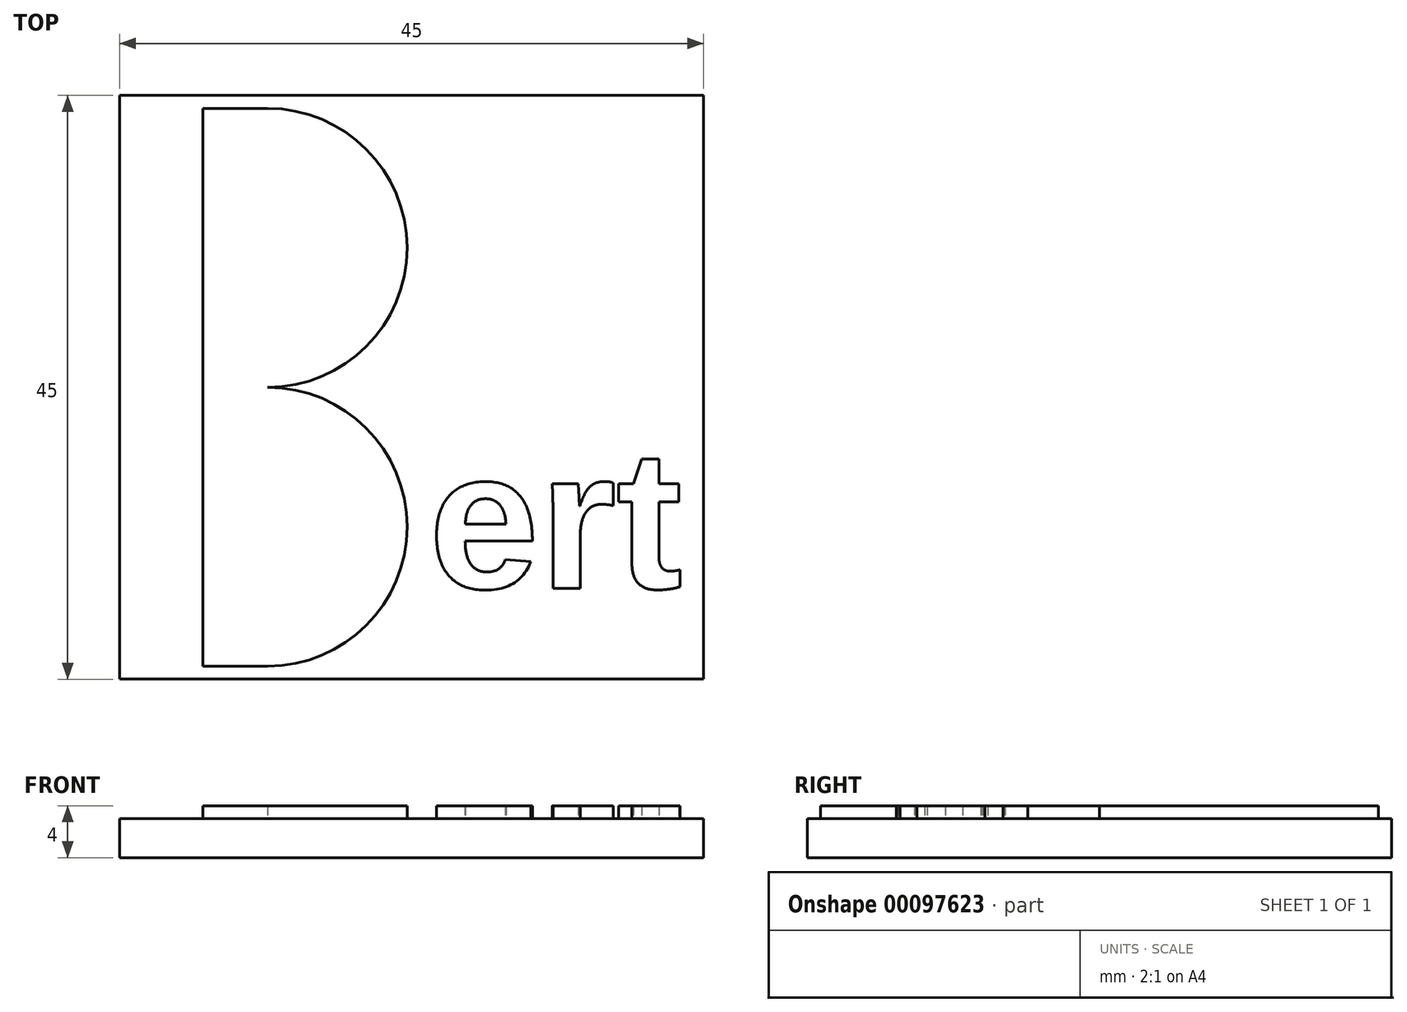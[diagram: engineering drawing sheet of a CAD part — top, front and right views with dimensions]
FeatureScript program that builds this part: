
annotation { "Feature Type Name" : "Feature", "Feature Type Description" : "" }
export const myFeature = defineFeature(function(context is Context, id is Id, definition is map)
    precondition{}
    {
        {
            var Q0;
            Q0=qCreatedBy(makeId("Top.planeOp"),FACE);
            var sketch = newSketch(context, id + "F0", { "sketchPlane" : qUnion([Q0])});
            skLineSegment(sketch, "E0.bottom", {"start": v(-39.88, 12.8) * mm, "end": v(5.12, 12.8) * mm});
            skLineSegment(sketch, "E0.top", {"start": v(-39.88, -32.2) * mm, "end": v(5.12, -32.2) * mm});
            skLineSegment(sketch, "E0.left", {"start": v(-39.88, 12.8) * mm, "end": v(-39.88, -32.2) * mm});
            skLineSegment(sketch, "E0.right", {"start": v(5.12, 12.8) * mm, "end": v(5.12, -32.2) * mm});
            skPoint(sketch, "E1", {"position": v(-33.48, 12.8) * mm});
            skLineSegment(sketch, "E2", {"start": v(-33.48, 11.8) * mm, "end": v(-33.48, -31.2) * mm});
            skLineSegment(sketch, "E3", {"start": v(-33.48, 11.8) * mm, "end": v(-28.48, 11.8) * mm});
            skLineSegment(sketch, "E4", {"start": v(-33.48, -31.2) * mm, "end": v(-28.48, -31.2) * mm});
            skArc(sketch, "E5", {"start": v(-28.48, -31.2) * mm, "mid": v(-17.73, -20.46) * mm, "end": v(-28.48, -9.7) * mm});
            skText(sketch, "E6", { "text": "ert", "fontName": "Arimo-Bold.ttf"});
            skArc(sketch, "E7", {"start": v(-28.48, -9.7) * mm, "mid": v(-17.73, 1.04) * mm, "end": v(-28.48, 11.8) * mm});
            skPoint(sketch, "E8.orphan", {"position": v(-28.48, 11.8) * mm});
            skPoint(sketch, "E9.orphan", {"position": v(-28.48, -9.7) * mm});
            const initialGuessF0  = {"E6": [-0.01605, -0.0252, 1, 0, 0.011]};
            skSetInitialGuess(sketch, initialGuessF0);
            skSolve(sketch);
        }
        {
            var Q0;
            Q0=makeQuery(id+"F0.imprint","IMPRINT",FACE,{"disambiguationData":[TD([[makeQuery(id+"F0.imprint","IMPRINT",EDGE,{"derivedFrom":sQuery(id+"F0.wireOp",EDGE,"E2")}),1.0]])]});
            var Q1;
            Q1=makeQuery(id+"F0.imprint","IMPRINT",FACE,{"disambiguationData":[TD([[makeQuery(id+"F0.imprint","IMPRINT",EDGE,{"derivedFrom":sQuery(id+"F0.wireOp",EDGE,"E0.bottom")}),-1.0]])]});
            var Q2;
            Q2=makeQuery(id+"F0.imprint","IMPRINT",FACE,{"disambiguationData":[TD([[makeQuery(id+"F0.imprint","IMPRINT",EDGE,{"derivedFrom":sQuery(id+"F0.wireOp",EDGE,"E6.sketch_text.stroke-0")}),-1.0]])]});
            var Q3;
            Q3=makeQuery(id+"F0.imprint","IMPRINT",FACE,{"disambiguationData":[TD([[makeQuery(id+"F0.imprint","IMPRINT",EDGE,{"derivedFrom":sQuery(id+"F0.wireOp",EDGE,"E6.sketch_text.stroke-18")}),-1.0]])]});
            var Q4;
            Q4=makeQuery(id+"F0.imprint","IMPRINT",FACE,{"disambiguationData":[TD([[makeQuery(id+"F0.imprint","IMPRINT",EDGE,{"derivedFrom":sQuery(id+"F0.wireOp",EDGE,"E6.sketch_text.stroke-35")}),-1.0]])]});
            var Q5;
            Q5=makeQuery(id+"F0.imprint","IMPRINT",FACE,{"disambiguationData":[TD([[makeQuery(id+"F0.imprint","IMPRINT",EDGE,{"derivedFrom":sQuery(id+"F0.wireOp",EDGE,"E6.sketch_text.stroke-13")}),1.0]])]});
            extrude(context, id + "F1", {"entities" : qUnion([Q0, Q1, Q2, Q3, Q4, Q5]), "oppositeDirection" : true, "depth" : 3 * mm});
        }
        {
            var Q0;
            Q0=makeQuery(id+"F0.imprint","IMPRINT",FACE,{"disambiguationData":[TD([[makeQuery(id+"F0.imprint","IMPRINT",EDGE,{"derivedFrom":sQuery(id+"F0.wireOp",EDGE,"E2")}),1.0]])]});
            var Q1;
            Q1=makeQuery(id+"F0.imprint","IMPRINT",FACE,{"disambiguationData":[TD([[makeQuery(id+"F0.imprint","IMPRINT",EDGE,{"derivedFrom":sQuery(id+"F0.wireOp",EDGE,"E6.sketch_text.stroke-0")}),-1.0]])]});
            var Q2;
            Q2=makeQuery(id+"F0.imprint","IMPRINT",FACE,{"disambiguationData":[TD([[makeQuery(id+"F0.imprint","IMPRINT",EDGE,{"derivedFrom":sQuery(id+"F0.wireOp",EDGE,"E6.sketch_text.stroke-18")}),-1.0]])]});
            var Q3;
            Q3=makeQuery(id+"F0.imprint","IMPRINT",FACE,{"disambiguationData":[TD([[makeQuery(id+"F0.imprint","IMPRINT",EDGE,{"derivedFrom":sQuery(id+"F0.wireOp",EDGE,"E6.sketch_text.stroke-35")}),-1.0]])]});
            extrude(context, id + "F2", {"entities" : qUnion([Q0, Q1, Q2, Q3]), "operationType" : NewBodyOperationType.ADD, "depth" : 1 * mm});
        }
    });
